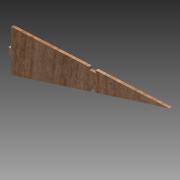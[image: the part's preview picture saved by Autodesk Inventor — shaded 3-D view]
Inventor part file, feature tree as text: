
AUTODESK INVENTOR PART (.ipt)
format: ipt  version: 2015 (Build 190159000, 159)  size: 134,656 bytes
history: native  units: in
note: dims shown in document units (in); Inventor stores cm internally (conversion verified against a paired STEP export)
features: sketch x4, extrude x3
ambient origin geometry x8: Origin, YZ Plane, XZ Plane, XY Plane, X Axis, Y Axis, Z Axis, Center Point
bodies: Solid1 (feature_tree)
feature tree (7):
  extrude  "Extrusion1"  Depth=0.125in TaperAngle=0.0deg
  extrude  "Extrusion3"  Depth=0.125in
  extrude  "Extrusion5"  Depth=0.3in
  sketch  "Sketch6"  dims[d34=0.125in d35=0.125in d36=0.3in d38=1.0in d39=0.0in d40=0.639in d41=0.4974in d43=1.042in d44=0.15in d45=3.802in d46=3.802in d47=0.15in d48=0.15in]
  sketch  "Sketch1"  dims[d0=1.959in d2=0.125in d3=0.0in]
  sketch  "Sketch3"  dims[d9=0.3in d11=0.125in]
  sketch  "Sketch5"  dims[d12=0.125in d13=0.0in d32=0.3in]
